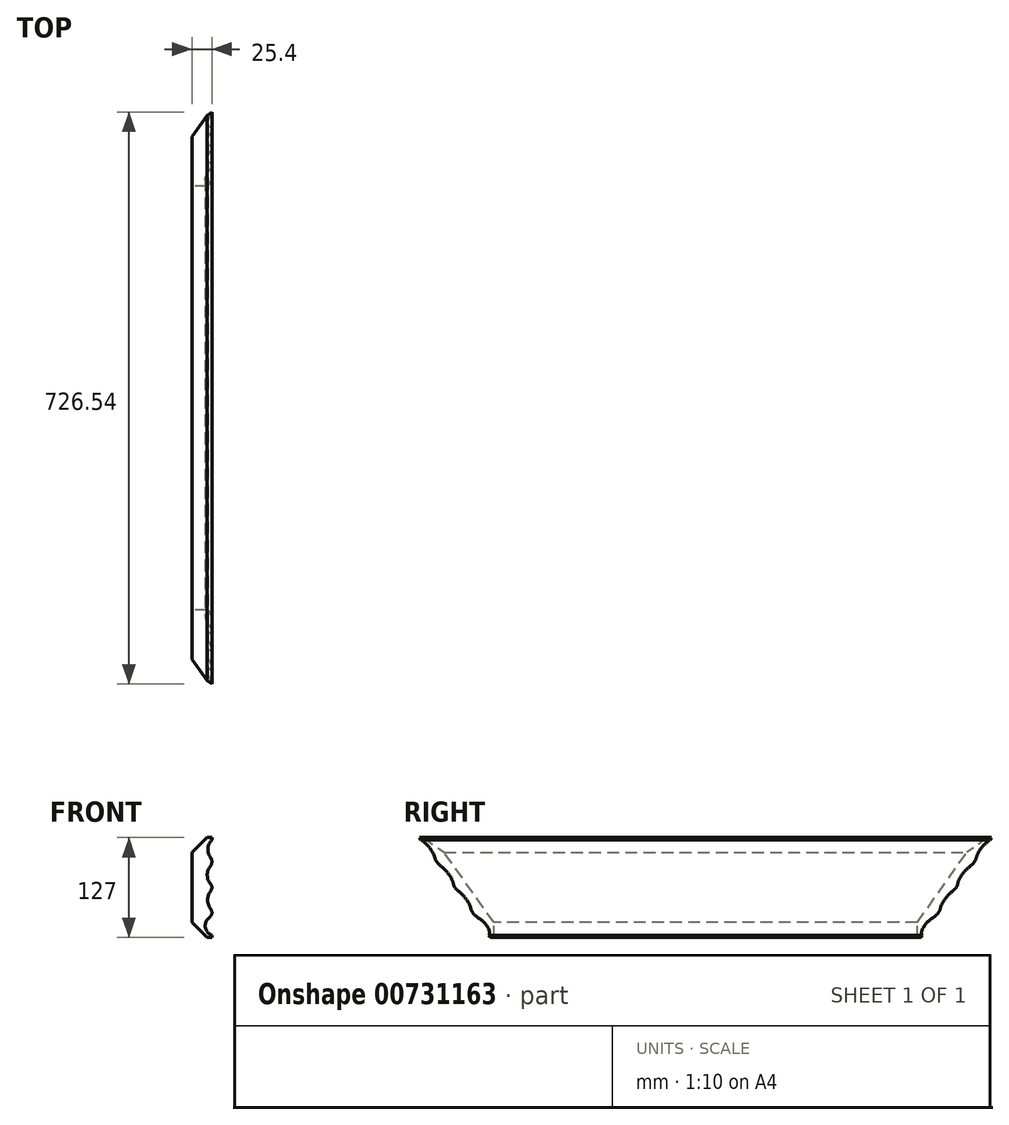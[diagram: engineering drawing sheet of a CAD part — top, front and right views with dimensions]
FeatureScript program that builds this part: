
annotation { "Feature Type Name" : "Feature", "Feature Type Description" : "" }
export const myFeature = defineFeature(function(context is Context, id is Id, definition is map)
    precondition{}
    {
        {
            var Q0;
            Q0=qCreatedBy(makeId("Front.planeOp"),FACE);
            var sketch = newSketch(context, id + "F0", { "sketchPlane" : qUnion([Q0])});
            skLineSegment(sketch, "E0.bottom", {"start": v(12.7, -63.5) * mm, "end": v(-12.7, -63.5) * mm});
            skLineSegment(sketch, "E0.top", {"start": v(12.7, 63.5) * mm, "end": v(-12.7, 63.5) * mm});
            skLineSegment(sketch, "E0.left", {"start": v(12.7, -63.5) * mm, "end": v(12.7, 63.5) * mm});
            skLineSegment(sketch, "E0.right", {"start": v(-12.7, -63.5) * mm, "end": v(-12.7, 63.5) * mm});
            skPoint(sketch, "E0.middle", {"position": v(0, 0) * mm});
            skSolve(sketch);
        }
        {
            var Q0;
            Q0=qSketchRegion(id+"F0",true);
            extrude(context, id + "F1", {"entities" : qUnion([Q0]), "endBound" : BoundingType.SYMMETRIC, "oppositeDirection" : true, "depth" : 762 * mm, "offsetDistance" : 25.4 * mm});
        }
        {
            var Q0;
            Q0=makeQuery(id+"F1.opExtrude","SWEPT_EDGE",EDGE,{"disambiguationData":[OSD([sQuery(id+"F0.wireOp",EDGE,"E0.top"),sQuery(id+"F0.wireOp",EDGE,"E0.right")])]});
            var Q1;
            Q1=makeQuery(id+"F1.opExtrude","SWEPT_EDGE",EDGE,{"disambiguationData":[OSD([sQuery(id+"F0.wireOp",EDGE,"E0.bottom"),sQuery(id+"F0.wireOp",EDGE,"E0.right")])]});
            chamfer(context, id + "F2", {"entities" : qUnion([Q0, Q1]), "width" : 19.05 * mm, "tangentPropagation" : true});
        }
        {
            var Q0;
            Q0=makeQuery(id+"F1.opExtrude","CAP_FACE",FACE,{"disambiguationData":[OSD([sQuery(id+"F0.wireOp",EDGE,"E0.bottom"),sQuery(id+"F0.wireOp",EDGE,"E0.top"),sQuery(id+"F0.wireOp",EDGE,"E0.left"),sQuery(id+"F0.wireOp",EDGE,"E0.right")])],"isStart":true});
            var sketch = newSketch(context, id + "F3", { "sketchPlane" : qUnion([Q0])});
            skArc(sketch, "E1", {"start": v(10.78, 27.27) * mm, "mid": v(12.7, 32.47) * mm, "end": v(11.06, 37.77) * mm});
            skArc(sketch, "E2", {"start": v(9.4, -38.33) * mm, "mid": v(12.61, -33.04) * mm, "end": v(11.1, -27.05) * mm});
            skArc(sketch, "E3", {"start": v(11.31, -4.03) * mm, "mid": v(12.7, 0.16) * mm, "end": v(11.12, 4.27) * mm});
            skArc(sketch, "E4", {"start": v(9.4, -38.33) * mm, "mid": v(4.3, -50.48) * mm, "end": v(12.7, -60.62) * mm});
            skLineSegment(sketch, "E5", {"start": v(12.7, 63.5) * mm, "end": v(12.7, -63.5) * mm});
            skArc(sketch, "E6.trimOffspring", {"start": v(11.31, -4.03) * mm, "mid": v(7.31, -15.5) * mm, "end": v(11.1, -27.05) * mm});
            skArc(sketch, "E7.trimOffspring", {"start": v(10.78, 27.27) * mm, "mid": v(6.78, 15.7) * mm, "end": v(11.12, 4.27) * mm});
            skArc(sketch, "E8.trimOffspring", {"start": v(12.7, 60.57) * mm, "mid": v(7.73, 49.47) * mm, "end": v(11.06, 37.77) * mm});
            skSolve(sketch);
        }
        {
            var Q0;
            {var subQ0=sQuery(id+"F3.wireOp",EDGE,"E8.trimOffspring");Q0=makeQuery(id+"F3.imprint","IMPRINT",FACE,{"disambiguationData":[TD([[makeQuery(id+"F3.imprint","IMPRINT",EDGE,{"derivedFrom":subQ0}),1.0]])]});}
            var Q1;
            {var subQ0=sQuery(id+"F3.wireOp",EDGE,"E7.trimOffspring");Q1=makeQuery(id+"F3.imprint","IMPRINT",FACE,{"disambiguationData":[TD([[makeQuery(id+"F3.imprint","IMPRINT",EDGE,{"derivedFrom":subQ0}),1.0]])]});}
            var Q2;
            {var subQ0=sQuery(id+"F3.wireOp",EDGE,"E6.trimOffspring");Q2=makeQuery(id+"F3.imprint","IMPRINT",FACE,{"disambiguationData":[TD([[makeQuery(id+"F3.imprint","IMPRINT",EDGE,{"derivedFrom":subQ0}),1.0]])]});}
            var Q3;
            {var subQ0=sQuery(id+"F3.wireOp",EDGE,"E4");Q3=makeQuery(id+"F3.imprint","IMPRINT",FACE,{"disambiguationData":[TD([[makeQuery(id+"F3.imprint","IMPRINT",EDGE,{"derivedFrom":subQ0}),1.0]])]});}
            extrude(context, id + "F4", {"entities" : qUnion([Q0, Q1, Q2, Q3]), "operationType" : NewBodyOperationType.REMOVE, "endBound" : BoundingType.THROUGH_ALL, "oppositeDirection" : true, "depth" : 25.4 * mm, "offsetDistance" : 25.4 * mm});
        }
        {
            var Q0;
            Q0=makeQuery(id+"F2.opChamfer","BLEND_FACE",FACE,{"disambiguationData":[OSD([sQuery(id+"F0.wireOp",EDGE,"E0.top"),sQuery(id+"F0.wireOp",EDGE,"E0.right")])]});
            var sketch = newSketch(context, id + "F5", { "sketchPlane" : qUnion([Q0])});
            skLineSegment(sketch, "E9.0.0", {"start": v(-381, 53.88) * mm, "end": v(-381, 49.4) * mm});
            skLineSegment(sketch, "E9.0.1", {"start": v(-381, 49.4) * mm, "end": v(381, 49.4) * mm});
            skLineSegment(sketch, "E9.0.2", {"start": v(381, 49.4) * mm, "end": v(381, 53.88) * mm});
            skLineSegment(sketch, "E9.0.3", {"start": v(381, 53.88) * mm, "end": v(-381, 53.88) * mm});
            skLineSegment(sketch, "E10", {"start": v(-381, 53.88) * mm, "end": v(-248.65, -78.47) * mm});
            skLineSegment(sketch, "E11", {"start": v(-248.65, -78.47) * mm, "end": v(-381, -78.47) * mm});
            skLineSegment(sketch, "E12", {"start": v(-381, 49.4) * mm, "end": v(-381, -78.47) * mm});
            skLineSegment(sketch, "E13", {"start": v(381, 49.4) * mm, "end": v(381, -52.89) * mm});
            skLineSegment(sketch, "E14", {"start": v(381, -52.89) * mm, "end": v(238.77, -52.89) * mm});
            skLineSegment(sketch, "E15", {"start": v(345.54, 53.88) * mm, "end": v(238.77, -52.89) * mm});
            skSolve(sketch);
        }
        {
            var Q0;
            {var subQ4=sQuery(id+"F5.wireOp",EDGE,"E14");Q0=makeQuery(id+"F5.imprint","IMPRINT",FACE,{"disambiguationData":[TD([[makeQuery(id+"F5.imprint","IMPRINT",EDGE,{"derivedFrom":subQ4}),-1.0]])]});}
            var Q1;
            {var subQ1=sQuery(id+"F5.wireOp",EDGE,"E9.0.1");var subQ3=sQuery(id+"F5.wireOp",EDGE,"E15");var subQ4=makeQuery(id+"F5.imprint","INTERSECT",VERTEX,{"derivedFrom":[subQ1,subQ3]});Q1=makeQuery(id+"F5.imprint","IMPRINT",FACE,{"disambiguationData":[TD([[makeQuery(id+"F5.imprint","IMPRINT",EDGE,{"disambiguationData":[TD([[subQ4,-1.0]])],"derivedFrom":subQ1}),-1.0]])]});}
            var Q2;
            {var subQ0=sQuery(id+"F5.wireOp",EDGE,"E9.0.2");Q2=makeQuery(id+"F5.imprint","IMPRINT",FACE,{"disambiguationData":[TD([[makeQuery(id+"F5.imprint","IMPRINT",EDGE,{"derivedFrom":subQ0}),1.0]])]});}
            var Q3;
            {var subQ0=sQuery(id+"F5.wireOp",EDGE,"E11");Q3=makeQuery(id+"F5.imprint","IMPRINT",FACE,{"disambiguationData":[TD([[makeQuery(id+"F5.imprint","IMPRINT",EDGE,{"derivedFrom":subQ0}),-1.0]])]});}
            var Q4;
            {var subQ1=sQuery(id+"F5.wireOp",EDGE,"E9.0.1");var subQ3=sQuery(id+"F5.wireOp",EDGE,"E10");var subQ4=makeQuery(id+"F5.imprint","INTERSECT",VERTEX,{"derivedFrom":[subQ1,subQ3]});Q4=makeQuery(id+"F5.imprint","IMPRINT",FACE,{"disambiguationData":[TD([[makeQuery(id+"F5.imprint","IMPRINT",EDGE,{"disambiguationData":[TD([[subQ4,1.0]])],"derivedFrom":subQ1}),-1.0]])]});}
            var Q5;
            {var subQ0=sQuery(id+"F5.wireOp",EDGE,"E9.0.0");Q5=makeQuery(id+"F5.imprint","IMPRINT",FACE,{"disambiguationData":[TD([[makeQuery(id+"F5.imprint","IMPRINT",EDGE,{"derivedFrom":subQ0}),1.0]])]});}
            extrude(context, id + "F6", {"entities" : qUnion([Q0, Q1, Q2, Q3, Q4, Q5]), "operationType" : NewBodyOperationType.REMOVE, "endBound" : BoundingType.THROUGH_ALL, "oppositeDirection" : true, "depth" : 25.4 * mm, "offsetDistance" : 25.4 * mm});
        }
    });
